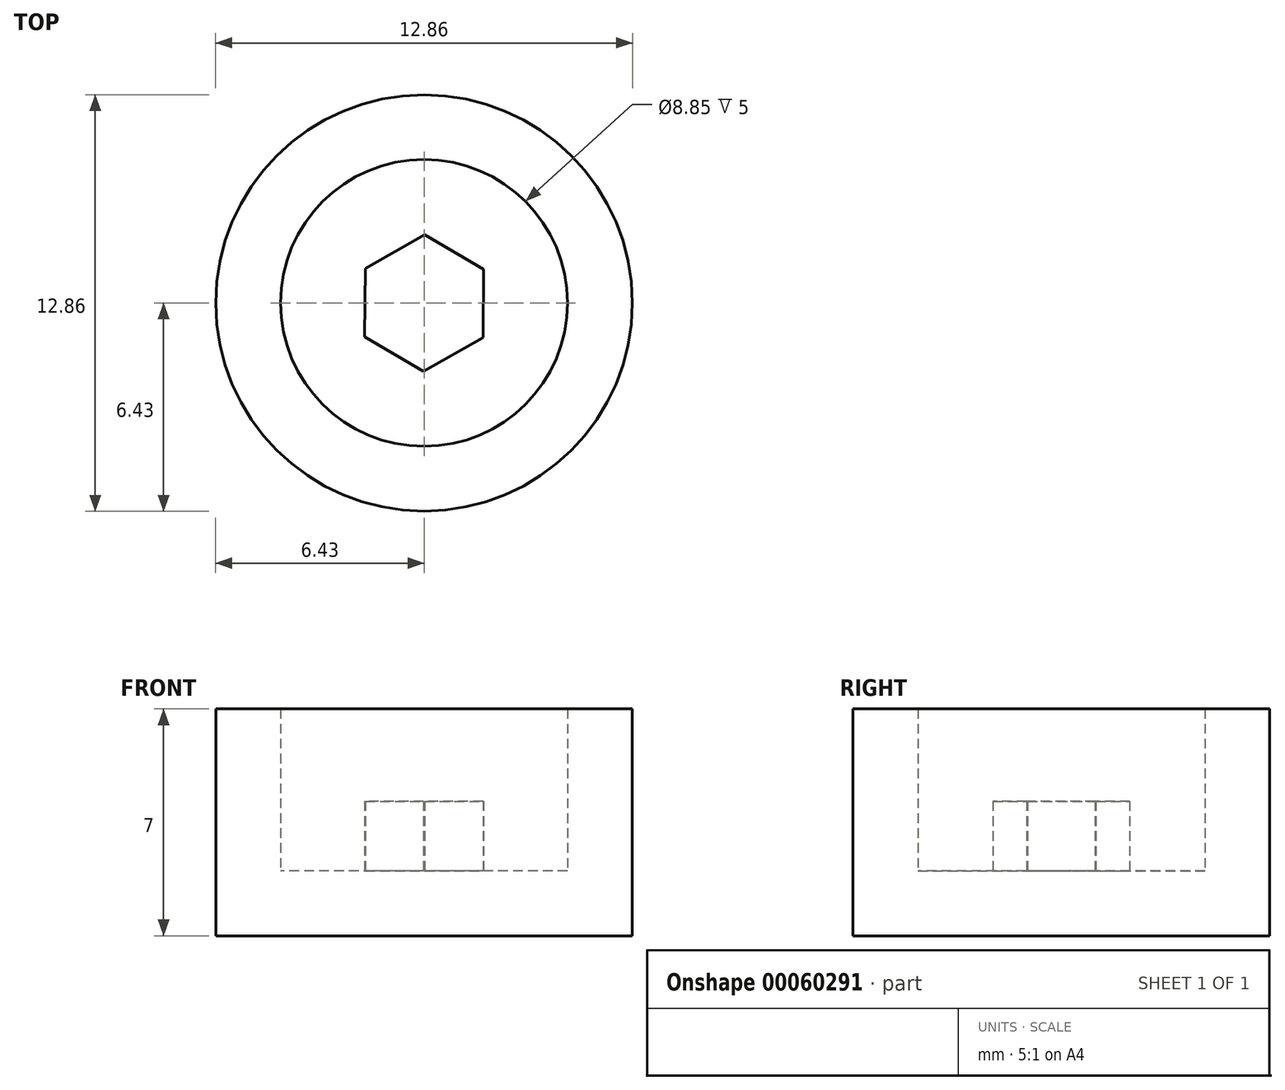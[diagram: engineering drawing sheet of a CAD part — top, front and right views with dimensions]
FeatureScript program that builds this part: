
annotation { "Feature Type Name" : "Feature", "Feature Type Description" : "" }
export const myFeature = defineFeature(function(context is Context, id is Id, definition is map)
    precondition{}
    {
        {
            var Q0;
            Q0=qCreatedBy(makeId("Top.planeOp"),FACE);
            var sketch = newSketch(context, id + "F0", { "sketchPlane" : qUnion([Q0])});
            skCircle(sketch, "E0", {"center": v(0, 0) * mm, "radius": 6.42 * mm});
            skCircle(sketch, "E1", {"center": v(0, 0) * mm, "radius": 4.42 * mm});
            skCircle(sketch, "E2.cCircle", {"center": v(0, 0) * mm, "radius": 1.82 * mm, "construction": true});
            skLineSegment(sketch, "E2.0", {"start": v(-0.02, -2.1) * mm, "end": v(-1.83, -1.04) * mm});
            skLineSegment(sketch, "E2.1", {"start": v(-1.83, -1.04) * mm, "end": v(-1.82, 1.07) * mm});
            skLineSegment(sketch, "E2.2", {"start": v(-1.82, 1.07) * mm, "end": v(0.02, 2.1) * mm});
            skLineSegment(sketch, "E2.3", {"start": v(0.02, 2.1) * mm, "end": v(1.83, 1.04) * mm});
            skLineSegment(sketch, "E2.4", {"start": v(1.83, 1.04) * mm, "end": v(1.82, -1.07) * mm});
            skLineSegment(sketch, "E2.5", {"start": v(1.82, -1.07) * mm, "end": v(-0.02, -2.1) * mm});
            skPoint(sketch, "E2.0.midPoint", {"position": v(-0.93, -1.57) * mm});
            skSolve(sketch);
        }
        {
            var Q0;
            Q0=makeQuery(id+"F0.imprint","IMPRINT",FACE,{"disambiguationData":[TD([[makeQuery(id+"F0.imprint","IMPRINT",EDGE,{"derivedFrom":sQuery(id+"F0.wireOp",EDGE,"E1")}),1.0]])]});
            extrude(context, id + "F1", {"entities" : qUnion([Q0]), "depth" : 2 * mm});
        }
        {
            var Q0;
            Q0=makeQuery(id+"F0.imprint","IMPRINT",FACE,{"disambiguationData":[TD([[makeQuery(id+"F0.imprint","IMPRINT",EDGE,{"derivedFrom":sQuery(id+"F0.wireOp",EDGE,"E0")}),1.0]])]});
            extrude(context, id + "F2", {"entities" : qUnion([Q0]), "operationType" : NewBodyOperationType.ADD, "depth" : 7 * mm});
        }
        {
            var Q0;
            Q0=makeQuery(id+"F0.imprint","IMPRINT",FACE,{"disambiguationData":[TD([[makeQuery(id+"F0.imprint","IMPRINT",EDGE,{"derivedFrom":sQuery(id+"F0.wireOp",EDGE,"E2.0")}),-1.0]])]});
            extrude(context, id + "F3", {"entities" : qUnion([Q0]), "operationType" : NewBodyOperationType.ADD, "depth" : 4.15 * mm});
        }
    });
